# Revit family: PVB Professional Series - Mini Standard Valve Box
name_source: partatom
category: Acessórios do tubo
units: mm (PartAtom-declared; Revit-internal decimal feet)

## family parameters
Com base no plano de trabalho = Não
Compartilhado = Não
Corte com vazios quando carregada = Não
Cota do conector redondo = Utilizar diâmetro
Número OmniClass = 23.60.00.00
Sempre na vertical = Sim
Tipo de parte = Normal
Título OmniClass = General Purpose: Services

## types (1)
- Mini Standard Valve Box
    Bottom = 46
    DDT1 = 0
    DDT2 = 19
    DDT3 = 23
    DDT4 = 0
    DDT5 = 2
    DDT6 = 2
    Descrição = PVB Professional Series - Mini Standard Valve Box
    Elevação padrão = 0
    Height = 25
    Modelo = STDEXT
    Plastic 1 = Black
    Plastic 2 = Green
    R = 4
    RainBird: Code = A12516
    RainBird: Description = PVB Professional Series - Mini Standard Valve Box
    RainBird: Product Link = https://www.rainbird.com
    SupportProjetos: Level of Detail = LOD300
    SupportProjetos: Reviw = R00
    Top = 38
    Top Length = 38
    Top Width = 24
    URL = https://www.rainbird.com
